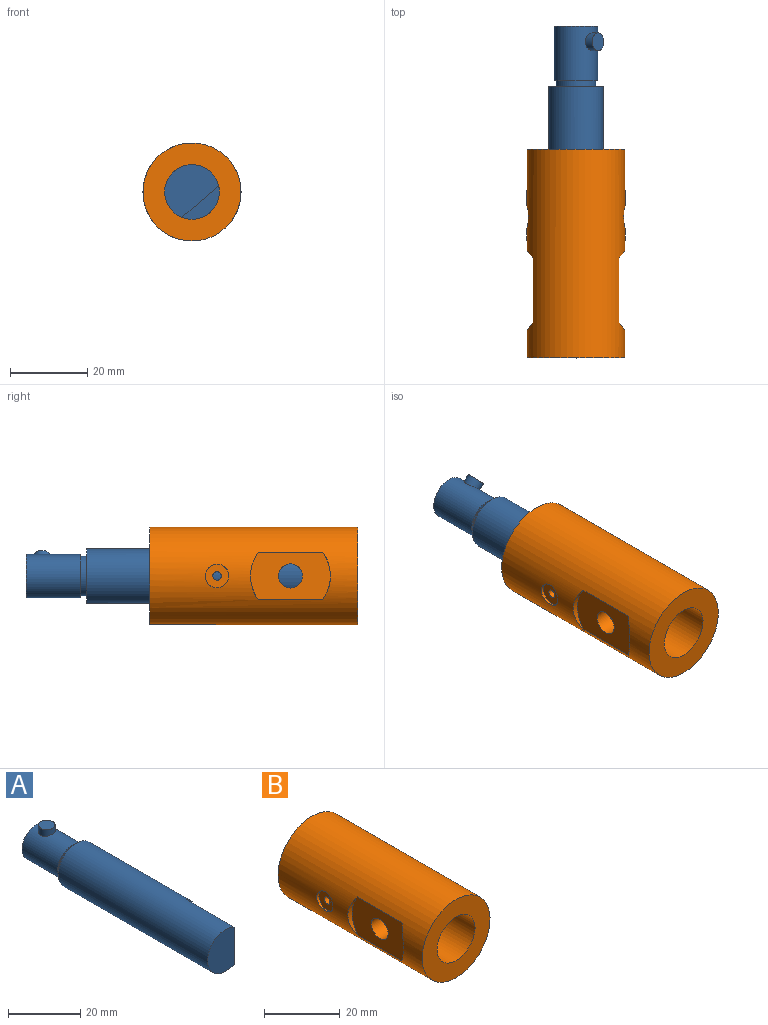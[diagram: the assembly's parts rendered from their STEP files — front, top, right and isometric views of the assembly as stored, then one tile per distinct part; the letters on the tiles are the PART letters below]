
ASSEMBLY  parts=2 mates=1
PART A: 11 faces, bbox 14.2x74.2x14.6 mm
  f0: cylinder r=5.6mm len=14mm, axis (0,-1,0), area 475.6mm2, adj f7,f8,f9
  f1: cylinder r=7.1mm len=58.5mm, axis (0,-1,0), area 2316.3mm2, adj f2,f3,f4,f5
  f2: plane 14.2x10.4mm, normal (0,-1,0), area 124.3mm2, adj f1,f3
  f3: plane 19x12.57mm, normal (1,0,0), area 238.9mm2, adj f1,f2,f4
  f4: plane 12.57x3.8mm, normal (0,-1,0), area 34.1mm2, adj f1,f3
  f5: plane 14.2x14.2mm, normal (0,1,0), area 75mm2, adj f1,f6
  f6: cylinder r=5.15mm len=10.3mm, axis (0,-1,0), area 55mm2, adj f5,f8
  f7: plane 11.2x11.2mm, normal (0,1,0), area 98.5mm2, adj f0
  f8: plane 11.2x11.2mm, normal (0,-1,0), area 15.2mm2, adj f0,f6
  f9: cylinder r=2.3mm len=4.6mm, axis (0,0,-1), area 31mm2, adj f0,f10
  f10: plane 4.6x4.6mm, normal (0,0,1), area 16.6mm2, adj f9
PART B: 22 faces, bbox 25.4x54x25.4 mm
  f0: cylinder r=12.7mm len=54mm, axis (0,1,0), area 3692.1mm2, adj f4,f5,f6,f7,f8,f9,f13,f14
  f1: cylinder r=1.1mm len=4.79mm, axis (1,0,0), area 32.8mm2, adj f3,f10
  f2: cylinder r=3.12mm len=6.25mm, axis (1,0,0), area 85.6mm2, adj f3,f8
  f3: cylinder r=7.1mm len=54mm, axis (0,1,0), area 2338.3mm2, adj f1,f2,f4,f5,f11,f12
  f4: plane 25.4x25.4mm, normal (0,-1,0), area 348.3mm2, adj f0,f3
  f5: plane 25.4x25.3mm, normal (0,1,0), area 339.4mm2, adj f0,f3,f19,f20,f21
  f6: cylinder r=10.35mm len=12.34mm, axis (-1,0,0), area 13.9mm2, adj f0,f8
  f7: cylinder r=10.35mm len=12.34mm, axis (-1,0,0), area 13.9mm2, adj f0,f8
  f8: plane 20.7x12.34mm, normal (-1,0,0), area 208.7mm2, adj f0,f2,f6,f7
  f9: cylinder r=3.05mm len=6.1mm, axis (-1,0,0), area 13.7mm2, adj f0,f10
  f10: plane 6.1x6.1mm, normal (-1,0,0), area 25.4mm2, adj f1,f9
  f11: cylinder r=1.1mm len=4.79mm, axis (-1,0,0), area 32.8mm2, adj f3,f17
  f12: cylinder r=3.12mm len=6.25mm, axis (-1,0,0), area 85.5mm2, adj f3,f15
  f13: cylinder r=10.35mm len=12.34mm, axis (1,0,0), area 13.9mm2, adj f0,f15
  f14: cylinder r=10.35mm len=12.34mm, axis (1,0,0), area 13.9mm2, adj f0,f15
  f15: plane 20.7x12.34mm, normal (1,0,0), area 208.7mm2, adj f0,f12,f13,f14
  f16: cylinder r=3.05mm len=6.1mm, axis (1,0,0), area 13.7mm2, adj f0,f17
  f17: plane 6.1x6.1mm, normal (1,0,0), area 25.4mm2, adj f11,f16
  f18: cylinder r=1.62mm len=3.25mm, axis (0,0,-1), area 14mm2, adj f0,f19,f20,f21
  f19: plane 16.88x2.7mm, normal (-1,0,0), area 45.5mm2, adj f0,f5,f18,f21
  f20: plane 16.88x2.7mm, normal (1,0,0), area 45.5mm2, adj f0,f5,f18,f21
  f21: plane 18.5x3.25mm, normal (0,0,-1), area 59mm2, adj f5,f18,f19,f20
PLACE A rot(axis=(0,1,0),49.6deg) t=(-0.21,38.72,0.05)mm
PLACE B t=(-0.21,26.92,0.05)mm fixed
MATE cylindrical B.f3 <-> A.f1  axis (0,1,0) through (-0.21,-27.08,0.05)mm
